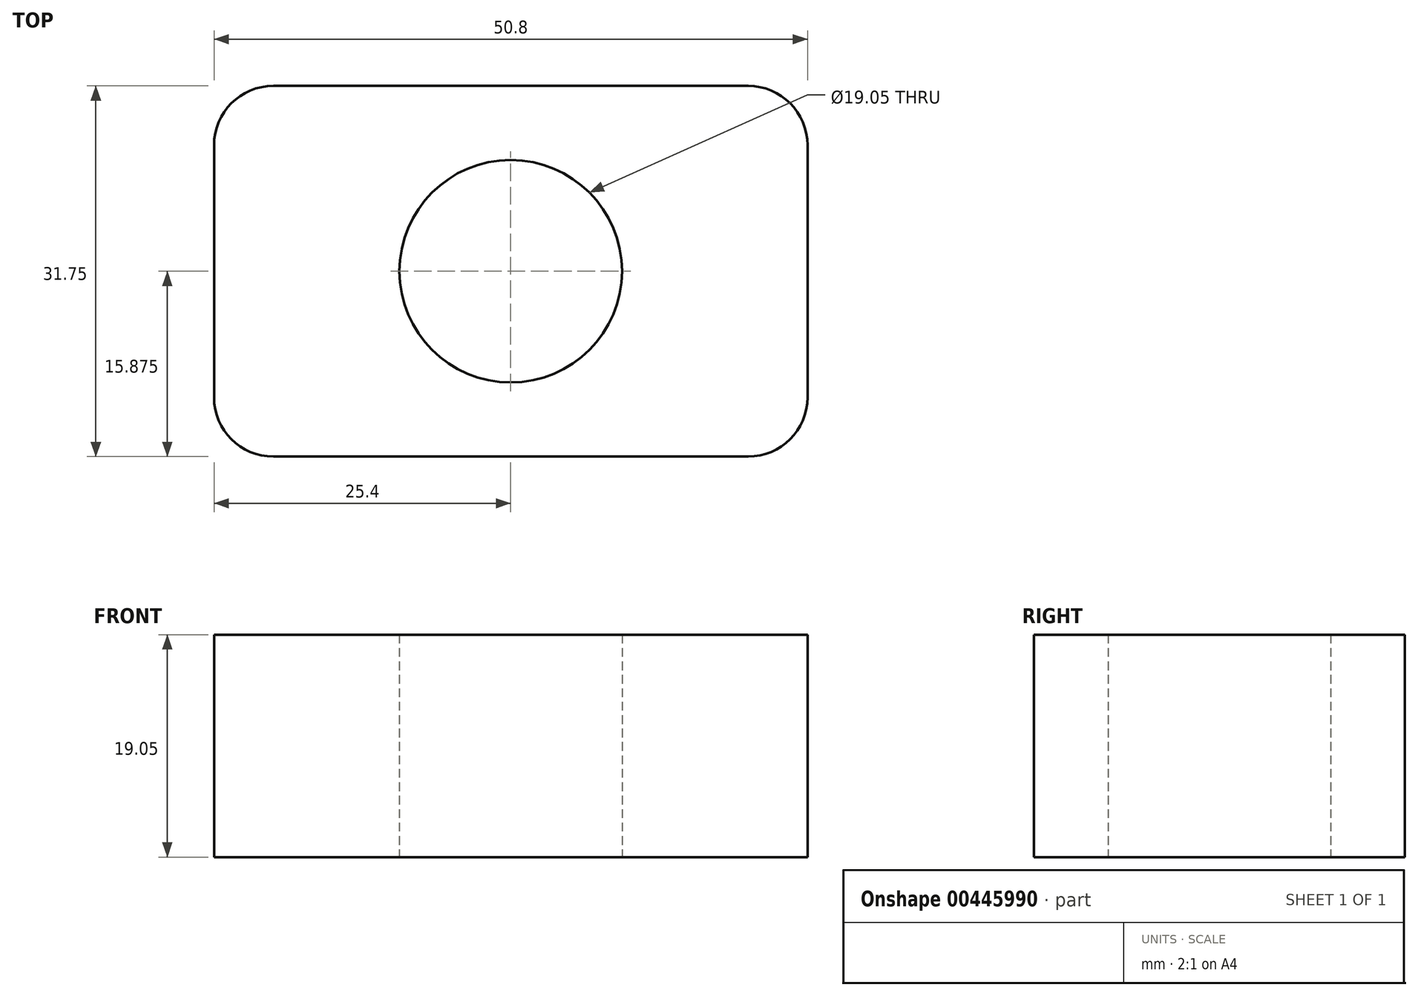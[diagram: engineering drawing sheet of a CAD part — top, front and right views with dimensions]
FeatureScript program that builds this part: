
annotation { "Feature Type Name" : "Feature", "Feature Type Description" : "" }
export const myFeature = defineFeature(function(context is Context, id is Id, definition is map)
    precondition{}
    {
        {
            var Q0;
            Q0=qCreatedBy(makeId("Top.planeOp"),FACE);
            var sketch = newSketch(context, id + "F0", { "sketchPlane" : qUnion([Q0])});
            skLineSegment(sketch, "E0.bottom", {"start": v(0, 0) * mm, "end": v(50.8, 0) * mm});
            skLineSegment(sketch, "E0.top", {"start": v(0, 31.75) * mm, "end": v(50.8, 31.75) * mm});
            skLineSegment(sketch, "E0.left", {"start": v(0, 0) * mm, "end": v(0, 31.75) * mm});
            skLineSegment(sketch, "E0.right", {"start": v(50.8, 0) * mm, "end": v(50.8, 31.75) * mm});
            skLineSegment(sketch, "E1", {"start": v(0, 31.75) * mm, "end": v(50.8, 0) * mm, "construction": true});
            skLineSegment(sketch, "E2", {"start": v(0, 0) * mm, "end": v(50.8, 31.75) * mm, "construction": true});
            skCircle(sketch, "E3", {"center": v(25.4, 15.87) * mm, "radius": 9.53 * mm});
            skSolve(sketch);
        }
        {
            var Q0;
            Q0=makeQuery(id+"F0.imprint","IMPRINT",FACE,{"disambiguationData":[TD([[makeQuery(id+"F0.imprint","IMPRINT",EDGE,{"derivedFrom":sQuery(id+"F0.wireOp",EDGE,"E0.bottom")}),1.0]])]});
            extrude(context, id + "F1", {"entities" : qUnion([Q0]), "depth" : 19.05 * mm});
        }
        {
            var Q0;
            Q0=makeQuery(id+"F1.opExtrude","SWEPT_EDGE",EDGE,{"disambiguationData":[OSD([sQuery(id+"F0.wireOp",EDGE,"E0.bottom"),sQuery(id+"F0.wireOp",EDGE,"E0.right")])]});
            var Q1;
            Q1=makeQuery(id+"F1.opExtrude","SWEPT_EDGE",EDGE,{"disambiguationData":[OSD([sQuery(id+"F0.wireOp",EDGE,"E0.top"),sQuery(id+"F0.wireOp",EDGE,"E0.right")])]});
            var Q2;
            Q2=makeQuery(id+"F1.opExtrude","SWEPT_EDGE",EDGE,{"disambiguationData":[OSD([sQuery(id+"F0.wireOp",EDGE,"E0.bottom"),sQuery(id+"F0.wireOp",EDGE,"E0.left")])]});
            var Q3;
            Q3=makeQuery(id+"F1.opExtrude","SWEPT_EDGE",EDGE,{"disambiguationData":[OSD([sQuery(id+"F0.wireOp",EDGE,"E0.top"),sQuery(id+"F0.wireOp",EDGE,"E0.left")])]});
            fillet(context, id + "F2", {"entities" : qUnion([Q0, Q1, Q2, Q3]), "radius" : 5.08 * mm, "tangentPropagation" : true, "allowEdgeOverflow" : false});
        }
    });
